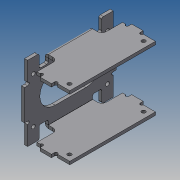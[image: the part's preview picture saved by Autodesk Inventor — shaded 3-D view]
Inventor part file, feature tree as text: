
AUTODESK INVENTOR PART (.ipt)
format: ipt  version: 2017 (Build 210142000, 142)  size: 261,632 bytes
history: native  units: mm
features: other x3, sketch x1, extrude x1
ambient origin geometry x8: Origin, YZ Plane, XZ Plane, XY Plane, X Axis, Y Axis, Z Axis, Center Point
bodies: Body1 (feature_tree)
feature tree (5):
  other  "Sólido1"
  sketch  "Boceto1"  dims[d0=4.0mm d1=40.0mm d2=2.0mm d5=2.0mm d9=15.0mm d10=20.0mm d11=75.8mm d13=120.0mm d14=58.0mm d15=23.0mm d16=4.0mm d17=4.0mm d18=0.0mm d19=4.0mm d20=2.0mm d21=8.0mm d22=4.0mm d23=90.0deg d24=0.1mm d25=4.0mm d26=2.0mm d27=8.0mm d28=4.0mm d29=90.0deg d30=0.1mm d31=8.0mm d32=7.5mm d33=15.0mm d34=5.0mm d35=10.0mm d36=7.5mm d37=40.0mm d38=20.0mm d39=12.0mm d40=4.0mm d41=6.0mm d42=2.0mm d43=6.0mm]
  extrude  "Extrusión1"  Depth=40.0mm
  other  "Pliegue1"
  other  "Pliegue2"
